# Revit family: SC Duplex 12 fibers
name_source: partatom
category: Installations électriques
units: mm (PartAtom-declared; Revit-internal decimal feet)

## family parameters
Basée sur le plan de construction = Non
Conserver l'orientation des annotations = Non
Cote de connecteur circulaire = Utiliser le diamètre
Couper avec des vides une fois chargée = Non
Partagée = Non
Point de calcul de pièce = Non
Toujours verticalement = Oui
Type d'élément = Normal

## types (2) — shared parameters
Color = IDS_NOIR
Depth = 33.3 mm  [stored 0.109252 ft]
E-catalogue link = https://www.legrand.fr
ETIM class = EC001130
Function = Patch panels with optical connector Legrand
Height = 23 mm  [stored 0.0754593 ft]
Height of the connectors = 10 mm  [stored 0.0328084 ft]
IK = IK04
IP = IP20
Number of connectors = 12
Opening height = 1 mm  [stored 0.00328084 ft]
Opening width = 6 mm  [stored 0.019685 ft]
Operating temperature = -10°C à 60°C
RAL Number = 9017
Storage temperature = -10°C à 60°C
Type of connector external = SC_DUPLEX
Type of connector interior = SC_DUPLEX
Width (mm) = 108.8 mm  [stored 0.356955 ft]
Width of the connectors = 26 mm  [stored 0.0853018 ft]
zero-valued in all types: Elévation par défaut

## per-type parameters (varying)
| type | Colour of the connectors | EAN | Fiber optic type | Legrand part number |
| SC Duplex block 12 fibers multimode | IDS_JAUNE | 3414970961839 | Multimode | 032121 |
| SC Duplex block 12 fibers monomode | IDS_BLEU | 3414970961679 | Single mode | 032111 |

note: column(s) folded — value = type name in every type: BIM wording

note: [stored X ft] marks values corroborated as IEEE doubles in the binary element streams (Revit-internal decimal feet)
